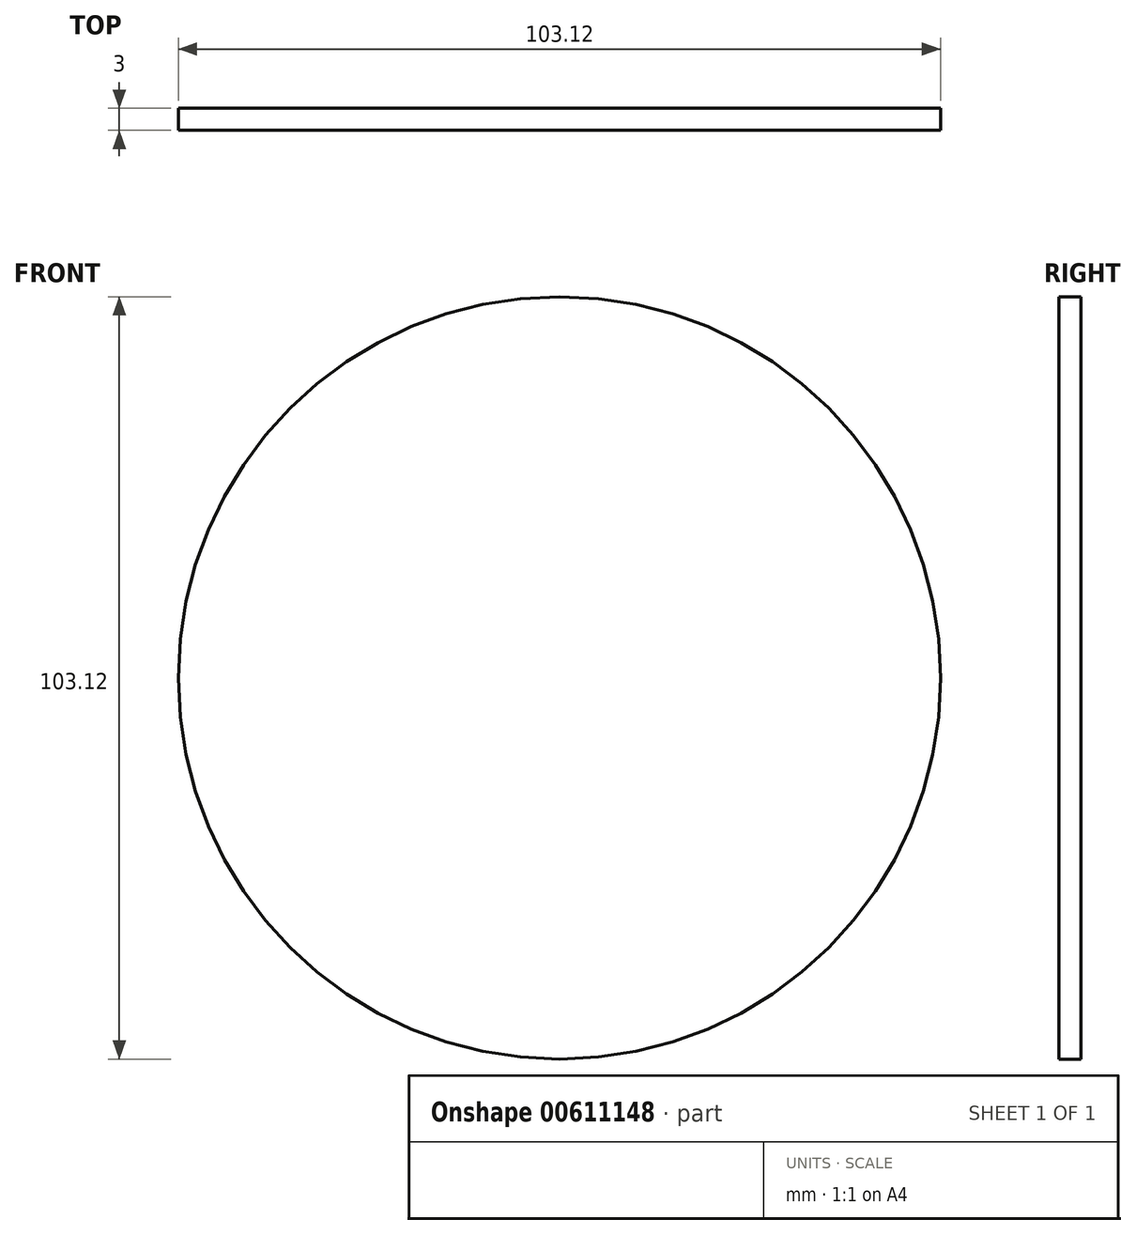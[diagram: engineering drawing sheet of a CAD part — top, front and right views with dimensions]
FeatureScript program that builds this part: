
annotation { "Feature Type Name" : "Feature", "Feature Type Description" : "" }
export const myFeature = defineFeature(function(context is Context, id is Id, definition is map)
    precondition{}
    {
        {
            var Q0;
            Q0=qCreatedBy(makeId("Front.planeOp"),FACE);
            var sketch = newSketch(context, id + "F0", { "sketchPlane" : qUnion([Q0])});
            skCircle(sketch, "E0", {"center": v(0, 0) * mm, "radius": 51.56 * mm});
            skSolve(sketch);
        }
        {
            var Q0;
            Q0=qSketchRegion(id+"F0",true);
            extrude(context, id + "F1", {"entities" : qUnion([Q0]), "depth" : 3 * mm, "offsetDistance" : 25.4 * mm});
        }
    });
